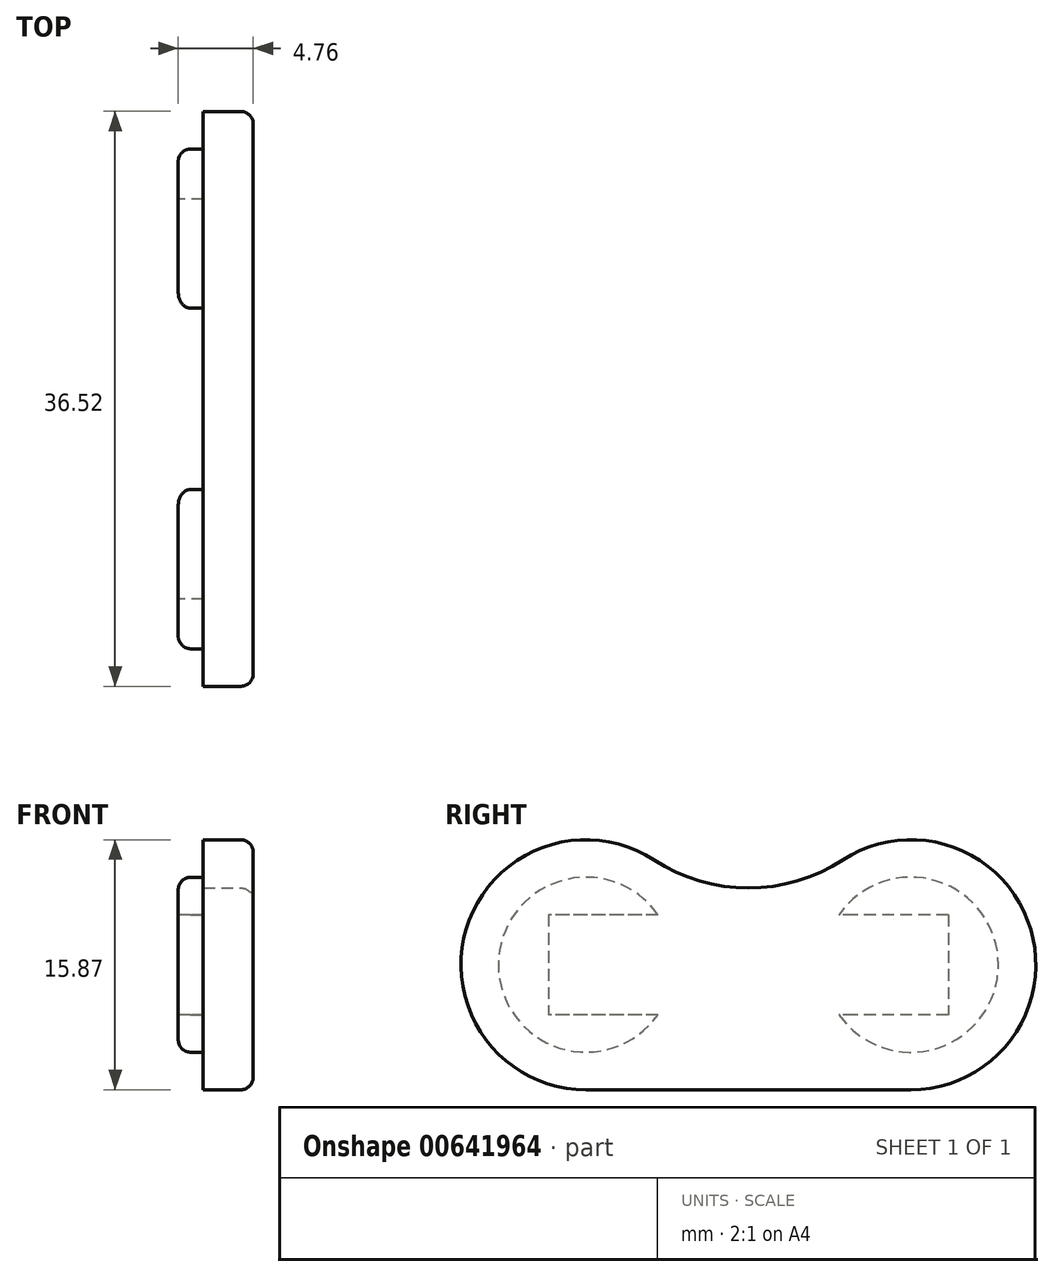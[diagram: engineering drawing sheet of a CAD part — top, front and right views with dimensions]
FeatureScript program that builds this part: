
annotation { "Feature Type Name" : "Feature", "Feature Type Description" : "" }
export const myFeature = defineFeature(function(context is Context, id is Id, definition is map)
    precondition{}
    {
        {
            var Q0;
            Q0=qCreatedBy(makeId("Right.planeOp"),FACE);
            var sketch = newSketch(context, id + "F0", { "sketchPlane" : qUnion([Q0])});
            skCircle(sketch, "E0", {"center": v(0, 0) * mm, "radius": 6.55 * mm});
            skCircle(sketch, "E1", {"center": v(0, 0) * mm, "radius": 8.73 * mm});
            skCircle(sketch, "E2", {"center": v(-10.32, -15.87) * mm, "radius": 5.56 * mm});
            skCircle(sketch, "E3", {"center": v(-10.32, -15.87) * mm, "radius": 7.94 * mm});
            skCircle(sketch, "E4", {"center": v(10.32, -15.87) * mm, "radius": 5.56 * mm});
            skCircle(sketch, "E5", {"center": v(10.32, -15.87) * mm, "radius": 7.94 * mm});
            skArc(sketch, "E6", {"start": v(-12.48, -8.24) * mm, "mid": v(-9.24, -5.77) * mm, "end": v(-8.55, -1.77) * mm});
            skArc(sketch, "E7", {"start": v(8.55, -1.77) * mm, "mid": v(9.24, -5.77) * mm, "end": v(12.48, -8.24) * mm});
            skLineSegment(sketch, "E8", {"start": v(-10.32, -23.81) * mm, "end": v(10.32, -23.81) * mm});
            skSolve(sketch);
        }
        {
            var Q0;
            Q0=makeQuery(id+"F0.imprint","IMPRINT",FACE,{"disambiguationData":[TD([[makeQuery(id+"F0.imprint","IMPRINT",EDGE,{"derivedFrom":sQuery(id+"F0.wireOp",EDGE,"E4")}),-1.0]])]});
            var Q1;
            Q1=makeQuery(id+"F0.imprint","IMPRINT",FACE,{"disambiguationData":[TD([[makeQuery(id+"F0.imprint","IMPRINT",EDGE,{"derivedFrom":sQuery(id+"F0.wireOp",EDGE,"E2")}),-1.0]])]});
            extrude(context, id + "F1", {"entities" : qUnion([Q0, Q1]), "depth" : 47.62 * mm, "offsetDistance" : 25.4 * mm});
        }
        {
            var Q0;
            Q0=makeQuery(id+"F0.imprint","IMPRINT",FACE,{"disambiguationData":[TD([[makeQuery(id+"F0.imprint","IMPRINT",EDGE,{"derivedFrom":sQuery(id+"F0.wireOp",EDGE,"E0")}),-1.0]])]});
            var Q1;
            {var subQ0=sQuery(id+"F0.wireOp",EDGE,"E3");var subQ1=sQuery(id+"F0.wireOp",EDGE,"E1");var subQ2=makeQuery(id+"F0.imprint","INTERSECT",VERTEX,{"disambiguationData":[OD(0.0)],"derivedFrom":[subQ1,subQ0]});Q1=makeQuery(id+"F0.imprint","IMPRINT",FACE,{"disambiguationData":[TD([[makeQuery(id+"F0.imprint","IMPRINT",EDGE,{"disambiguationData":[TD([[subQ2,-1.0]])],"derivedFrom":subQ1}),1.0]])]});}
            var Q2;
            {var subQ0=sQuery(id+"F0.wireOp",EDGE,"E5");var subQ1=sQuery(id+"F0.wireOp",EDGE,"E1");var subQ2=makeQuery(id+"F0.imprint","INTERSECT",VERTEX,{"disambiguationData":[OD(0.0)],"derivedFrom":[subQ1,subQ0]});Q2=makeQuery(id+"F0.imprint","IMPRINT",FACE,{"disambiguationData":[TD([[makeQuery(id+"F0.imprint","IMPRINT",EDGE,{"disambiguationData":[TD([[subQ2,-1.0]])],"derivedFrom":subQ1}),1.0]])]});}
            var Q3;
            {var subQ0=sQuery(id+"F0.wireOp",EDGE,"E6");Q3=makeQuery(id+"F0.imprint","IMPRINT",FACE,{"disambiguationData":[TD([[makeQuery(id+"F0.imprint","IMPRINT",EDGE,{"derivedFrom":subQ0}),-1.0]])]});}
            var Q4;
            {var subQ0=sQuery(id+"F0.wireOp",EDGE,"E7");Q4=makeQuery(id+"F0.imprint","IMPRINT",FACE,{"disambiguationData":[TD([[makeQuery(id+"F0.imprint","IMPRINT",EDGE,{"derivedFrom":subQ0}),-1.0]])]});}
            extrude(context, id + "F2", {"entities" : qUnion([Q0, Q1, Q2, Q3, Q4]), "operationType" : NewBodyOperationType.ADD, "depth" : 19.05 * mm, "offsetDistance" : 25.4 * mm});
        }
        {
            var Q0;
            Q0=makeQuery(id+"F1.opExtrude","CAP_FACE",FACE,{"disambiguationData":[OSD([sQuery(id+"F0.wireOp",EDGE,"E4"),sQuery(id+"F0.wireOp",EDGE,"E5")])],"isStart":false});
            var sketch = newSketch(context, id + "F3", { "sketchPlane" : qUnion([Q0])});
            skArc(sketch, "E9", {"start": v(-6, -9.22) * mm, "mid": v(0, -11) * mm, "end": v(6, -9.22) * mm});
            skCircle(sketch, "E10.0", {"center": v(10.32, -15.87) * mm, "radius": 7.94 * mm});
            skCircle(sketch, "E11.0", {"center": v(-10.32, -15.87) * mm, "radius": 7.94 * mm});
            skLineSegment(sketch, "E12.0", {"start": v(-10.32, -23.81) * mm, "end": v(10.32, -23.81) * mm});
            skSolve(sketch);
        }
        {
            var Q0;
            {var subQ0=sQuery(id+"F3.wireOp",EDGE,"E9");Q0=makeQuery(id+"F3.imprint","IMPRINT",FACE,{"disambiguationData":[TD([[makeQuery(id+"F3.imprint","IMPRINT",EDGE,{"derivedFrom":subQ0}),-1.0]])]});}
            extrude(context, id + "F4", {"entities" : qUnion([Q0]), "operationType" : NewBodyOperationType.ADD, "endBound" : BoundingType.UP_TO_NEXT, "oppositeDirection" : true, "depth" : 25.4 * mm, "offsetDistance" : 25.4 * mm});
        }
        {
            var Q0;
            {var subQ0=sQuery(id+"F0.wireOp",EDGE,"E5");var subQ1=sQuery(id+"F0.wireOp",EDGE,"E3");Q0=makeQuery(id+"F2.boolean.opBoolean","MERGE",FACE,{"derivedFrom":[makeQuery(id+"F1.opExtrude","CAP_FACE",FACE,{"disambiguationData":[OSD([sQuery(id+"F0.wireOp",EDGE,"E2"),subQ1])],"isStart":true}),makeQuery(id+"F1.opExtrude","CAP_FACE",FACE,{"disambiguationData":[OSD([sQuery(id+"F0.wireOp",EDGE,"E4"),subQ0])],"isStart":true}),makeQuery(id+"F2.opExtrude","CAP_FACE",FACE,{"disambiguationData":[OSD([sQuery(id+"F0.wireOp",EDGE,"E0"),sQuery(id+"F0.wireOp",EDGE,"E1"),subQ1,subQ0,sQuery(id+"F0.wireOp",EDGE,"E6"),sQuery(id+"F0.wireOp",EDGE,"E7"),sQuery(id+"F0.wireOp",EDGE,"E8")])],"isStart":true})]});}
            var sketch = newSketch(context, id + "F5", { "sketchPlane" : qUnion([Q0])});
            skLineSegment(sketch, "E13.bottom", {"start": v(4.37, -11.9) * mm, "end": v(-4.37, -11.9) * mm});
            skLineSegment(sketch, "E13.top", {"start": v(4.37, -20.64) * mm, "end": v(-4.37, -20.64) * mm});
            skLineSegment(sketch, "E13.left", {"start": v(4.37, -11.9) * mm, "end": v(4.37, -20.64) * mm});
            skLineSegment(sketch, "E13.right", {"start": v(-4.37, -11.9) * mm, "end": v(-4.37, -20.64) * mm});
            skPoint(sketch, "E13.middle", {"position": v(0, -16.27) * mm});
            skSolve(sketch);
        }
        {
            var Q0;
            {var subQ5=sQuery(id+"F5.wireOp",EDGE,"E13.bottom");Q0=makeQuery(id+"F5.imprint","IMPRINT",FACE,{"disambiguationData":[TD([[makeQuery(id+"F5.imprint","IMPRINT",EDGE,{"derivedFrom":subQ5}),1.0]])]});}
            extrude(context, id + "F6", {"entities" : qUnion([Q0]), "operationType" : NewBodyOperationType.REMOVE, "endBound" : BoundingType.THROUGH_ALL, "oppositeDirection" : true, "depth" : 25.4 * mm, "offsetDistance" : 25.4 * mm});
        }
        {
            var Q0;
            Q0=qCreatedBy(makeId("Front.planeOp"),FACE);
            var sketch = newSketch(context, id + "F7", { "sketchPlane" : qUnion([Q0])});
            skCircle(sketch, "E14", {"center": v(0, -16.27) * mm, "radius": 4.37 * mm});
            skCircle(sketch, "E15", {"center": v(47.63, -16.27) * mm, "radius": 4.37 * mm});
            skSolve(sketch);
        }
        {
            var Q0;
            Q0=makeQuery(id+"F7.imprint","IMPRINT",FACE,{"disambiguationData":[TD([[makeQuery(id+"F7.imprint","IMPRINT",EDGE,{"derivedFrom":sQuery(id+"F7.wireOp",EDGE,"E14")}),1.0]])]});
            var Q1;
            Q1=makeQuery(id+"F7.imprint","IMPRINT",FACE,{"disambiguationData":[TD([[makeQuery(id+"F7.imprint","IMPRINT",EDGE,{"derivedFrom":sQuery(id+"F7.wireOp",EDGE,"E15")}),1.0]])]});
            extrude(context, id + "F8", {"entities" : qUnion([Q0, Q1]), "operationType" : NewBodyOperationType.REMOVE, "oppositeDirection" : true, "depth" : 9.52 * mm, "offsetDistance" : 25.4 * mm, "hasSecondDirection" : true, "secondDirectionOppositeDirection" : false, "secondDirectionDepth" : 9.52 * mm});
        }
        {
            var Q0;
            Q0=makeQuery(id+"F6.boolean.opBoolean","COPY",FACE,{"derivedFrom":makeQuery(id+"F6.opExtrude","SWEPT_FACE",FACE,{"disambiguationData":[OSD([sQuery(id+"F5.wireOp",EDGE,"E13.bottom")])]})});
            var sketch = newSketch(context, id + "F9", { "sketchPlane" : qUnion([Q0])});
            skCircle(sketch, "E16", {"center": v(-0.51, 0) * mm, "radius": 4.37 * mm});
            skSolve(sketch);
        }
        {
            var Q0;
            {var subQ0=sQuery(id+"F9.wireOp",EDGE,"E16");var subQ1=makeQuery(id+"F6.boolean.opBoolean","COPY",EDGE,{"derivedFrom":makeQuery(id+"F6.opExtrude","CAP_EDGE",EDGE,{"disambiguationData":[OSD([sQuery(id+"F5.wireOp",EDGE,"E13.bottom")])],"isStart":true})});var subQ2=makeQuery(id+"F9.imprint","INTERSECT",VERTEX,{"disambiguationData":[OD(0.0)],"derivedFrom":[subQ1,subQ0]});Q0=makeQuery(id+"F9.imprint","IMPRINT",FACE,{"disambiguationData":[TD([[makeQuery(id+"F9.imprint","IMPRINT",EDGE,{"disambiguationData":[TD([[subQ2,1.0]])],"derivedFrom":subQ0}),1.0]])]});}
            var Q1;
            {var subQ0=sQuery(id+"F9.wireOp",EDGE,"E16");var subQ1=makeQuery(id+"F6.boolean.opBoolean","COPY",EDGE,{"derivedFrom":makeQuery(id+"F6.opExtrude","CAP_EDGE",EDGE,{"disambiguationData":[OSD([sQuery(id+"F5.wireOp",EDGE,"E13.bottom")])],"isStart":true})});var subQ2=makeQuery(id+"F9.imprint","INTERSECT",VERTEX,{"disambiguationData":[OD(0.0)],"derivedFrom":[subQ1,subQ0]});Q1=makeQuery(id+"F9.imprint","IMPRINT",FACE,{"disambiguationData":[TD([[makeQuery(id+"F9.imprint","IMPRINT",EDGE,{"disambiguationData":[TD([[subQ2,-1.0]])],"derivedFrom":subQ0}),1.0]])]});}
            extrude(context, id + "F10", {"entities" : qUnion([Q0, Q1]), "operationType" : NewBodyOperationType.REMOVE, "oppositeDirection" : true, "depth" : 9.52 * mm, "offsetDistance" : 25.4 * mm});
        }
        {
            var Q0;
            {var subQ0=sQuery(id+"F0.wireOp",EDGE,"E5");var subQ1=sQuery(id+"F0.wireOp",EDGE,"E3");Q0=makeQuery(id+"F2.boolean.opBoolean","MERGE",FACE,{"derivedFrom":[makeQuery(id+"F1.opExtrude","CAP_FACE",FACE,{"disambiguationData":[OSD([sQuery(id+"F0.wireOp",EDGE,"E2"),subQ1])],"isStart":true}),makeQuery(id+"F1.opExtrude","CAP_FACE",FACE,{"disambiguationData":[OSD([sQuery(id+"F0.wireOp",EDGE,"E4"),subQ0])],"isStart":true}),makeQuery(id+"F2.opExtrude","CAP_FACE",FACE,{"disambiguationData":[OSD([sQuery(id+"F0.wireOp",EDGE,"E0"),sQuery(id+"F0.wireOp",EDGE,"E1"),subQ1,subQ0,sQuery(id+"F0.wireOp",EDGE,"E6"),sQuery(id+"F0.wireOp",EDGE,"E7"),sQuery(id+"F0.wireOp",EDGE,"E8")])],"isStart":true})]});}
            var sketch = newSketch(context, id + "F11", { "sketchPlane" : qUnion([Q0])});
            skPoint(sketch, "E17", {"position": v(7.14, -7.94) * mm});
            skPoint(sketch, "E18", {"position": v(-7.14, -7.94) * mm});
            skSolve(sketch);
        }
        {
            var Q0;
            Q0=sQuery(id+"F11.wireOp",VERTEX,"E17");
            var Q1;
            Q1=sQuery(id+"F11.wireOp",VERTEX,"E18");
            var Q2;
            Q2=makeQuery(id+"F1.opExtrude","SWEPT_BODY",BODY,{"disambiguationData":[OSD([sQuery(id+"F0.wireOp",EDGE,"E2"),sQuery(id+"F0.wireOp",EDGE,"E3")])]});
            hole(context, id + "F12", {"style" : HoleStyle.SIMPLE, "endStyle" : HoleEndStyle.BLIND, "standardTappedOrClearance" : lookupTablePath({ "standard" : "ANSI", "engagement" : "75%", "pitch" : "32 tpi", "size" : "#6", "type" : "Tapped" }), "standardBlindInLast" : lookupTablePath({ "standard" : "ANSI", "engagement" : "75%", "pitch" : "32 tpi", "size" : "#6", "type" : "Tapped" }), "holeDiameter" : 2.7 * mm, "majorDiameter" : 3.5 * mm, "showTappedDepth" : true, "holeDepth" : 15.88 * mm, "isTappedThrough" : true, "tappedDepth" : 13.5 * mm, "tapClearance" : 3, "locations" : qUnion([Q0, Q1]), "scope" : qUnion([Q2])});
        }
        {
            var Q0;
            Q0=makeQuery(id+"F4.boolean.opBoolean","MERGE",FACE,{"derivedFrom":[makeQuery(id+"F1.opExtrude","CAP_FACE",FACE,{"disambiguationData":[OSD([sQuery(id+"F0.wireOp",EDGE,"E2"),sQuery(id+"F0.wireOp",EDGE,"E3")])],"isStart":false}),makeQuery(id+"F1.opExtrude","CAP_FACE",FACE,{"disambiguationData":[OSD([sQuery(id+"F0.wireOp",EDGE,"E4"),sQuery(id+"F0.wireOp",EDGE,"E5")])],"isStart":false}),makeQuery(id+"F4.opExtrude","CAP_FACE",FACE,{"disambiguationData":[OSD([sQuery(id+"F3.wireOp",EDGE,"E9"),sQuery(id+"F3.wireOp",EDGE,"E10.0"),sQuery(id+"F3.wireOp",EDGE,"E11.0"),sQuery(id+"F3.wireOp",EDGE,"E12.0")])],"isStart":true})]});
            var sketch = newSketch(context, id + "F13", { "sketchPlane" : qUnion([Q0])});
            skArc(sketch, "E19.0.0", {"start": v(-6, -9.22) * mm, "mid": v(-17.93, -13.62) * mm, "end": v(-10.32, -23.81) * mm});
            skLineSegment(sketch, "E19.0.1", {"start": v(-10.32, -23.81) * mm, "end": v(10.32, -23.81) * mm});
            skArc(sketch, "E19.0.2", {"start": v(10.32, -23.81) * mm, "mid": v(17.93, -13.62) * mm, "end": v(6, -9.22) * mm});
            skArc(sketch, "E19.0.3", {"start": v(6, -9.22) * mm, "mid": v(0, -11) * mm, "end": v(-6, -9.22) * mm});
            skSolve(sketch);
        }
        {
            var Q0;
            Q0=makeQuery(id+"F13.imprint","IMPRINT",FACE,{"disambiguationData":[TD([[makeQuery(id+"F13.imprint","IMPRINT",EDGE,{"derivedFrom":sQuery(id+"F13.wireOp",EDGE,"E19.0.0")}),1.0]])]});
            var Q1;
            {var subQ1=sQuery(id+"F0.wireOp",EDGE,"E2");Q1=makeQuery(id+"F13.imprint","IMPRINT",FACE,{"disambiguationData":[TD([[makeQuery(id+"F13.imprint","IMPRINT",EDGE,{"derivedFrom":makeQuery(id+"F1.opExtrude","CAP_EDGE",EDGE,{"disambiguationData":[OSD([subQ1])],"isStart":false})}),1.0]])]});}
            extrude(context, id + "F14", {"entities" : qUnion([Q0, Q1]), "operationType" : NewBodyOperationType.ADD, "depth" : 3.17 * mm, "offsetDistance" : 25.4 * mm});
        }
        {
            var Q0;
            Q0=qCreatedBy(makeId("Top.planeOp"),FACE);
            var sketch = newSketch(context, id + "F15", { "sketchPlane" : qUnion([Q0])});
            skLineSegment(sketch, "E20.bottom", {"start": v(47.62, 25.4) * mm, "end": v(-12.7, 25.4) * mm});
            skLineSegment(sketch, "E20.top", {"start": v(47.63, -25.4) * mm, "end": v(-12.7, -25.4) * mm});
            skLineSegment(sketch, "E20.left", {"start": v(47.63, 25.4) * mm, "end": v(47.63, -25.4) * mm});
            skLineSegment(sketch, "E20.right", {"start": v(-12.7, 25.4) * mm, "end": v(-12.7, -25.4) * mm});
            skSolve(sketch);
        }
        {
            var Q0;
            Q0=makeQuery(id+"F15.imprint","IMPRINT",FACE,{"disambiguationData":[TD([[makeQuery(id+"F15.imprint","IMPRINT",EDGE,{"derivedFrom":sQuery(id+"F15.wireOp",EDGE,"E20.bottom")}),1.0]])]});
            extrude(context, id + "F16", {"entities" : qUnion([Q0]), "operationType" : NewBodyOperationType.REMOVE, "oppositeDirection" : true, "depth" : 25.4 * mm, "offsetDistance" : 25.4 * mm, "hasSecondDirection" : true, "secondDirectionBound" : SecondDirectionBoundingType.THROUGH_ALL, "secondDirectionOppositeDirection" : false, "secondDirectionDepth" : 25.4 * mm});
        }
        {
            var Q0;
            Q0=makeQuery(id+"F13.imprint","IMPRINT",FACE,{"disambiguationData":[TD([[makeQuery(id+"F13.imprint","IMPRINT",EDGE,{"derivedFrom":sQuery(id+"F13.wireOp",EDGE,"E19.0.0")}),1.0]])]});
            var sketch = newSketch(context, id + "F17", { "sketchPlane" : qUnion([Q0])});
            skCircle(sketch, "E21.0", {"center": v(-10.32, -15.87) * mm, "radius": 5.56 * mm});
            skCircle(sketch, "E22.0", {"center": v(10.32, -15.87) * mm, "radius": 5.56 * mm});
            skSolve(sketch);
        }
        {
            var Q0;
            {var subQ0=sQuery(id+"F17.wireOp",EDGE,"E21.0");var subQ1=makeQuery(id+"F8.opExtrude","SWEPT_FACE",FACE,{"disambiguationData":[OSD([sQuery(id+"F7.wireOp",EDGE,"E15")])]});var subQ2=makeQuery(id+"F4.boolean.opBoolean","MERGE",FACE,{"derivedFrom":[makeQuery(id+"F1.opExtrude","CAP_FACE",FACE,{"disambiguationData":[OSD([sQuery(id+"F0.wireOp",EDGE,"E2"),sQuery(id+"F0.wireOp",EDGE,"E3")])],"isStart":false}),makeQuery(id+"F1.opExtrude","CAP_FACE",FACE,{"disambiguationData":[OSD([sQuery(id+"F0.wireOp",EDGE,"E4"),sQuery(id+"F0.wireOp",EDGE,"E5")])],"isStart":false}),makeQuery(id+"F4.opExtrude","CAP_FACE",FACE,{"disambiguationData":[OSD([sQuery(id+"F3.wireOp",EDGE,"E9"),sQuery(id+"F3.wireOp",EDGE,"E10.0"),sQuery(id+"F3.wireOp",EDGE,"E11.0"),sQuery(id+"F3.wireOp",EDGE,"E12.0")])],"isStart":true})]});var subQ3=makeQuery(id+"F17.imprint","INTERSECT",VERTEX,{"derivedFrom":[makeQuery(id+"F13.imprint","IMPRINT",EDGE,{"derivedFrom":makeQuery(id+"F8.boolean.opBoolean","INTERSECT",EDGE,{"disambiguationData":[OD(0.0)],"derivedFrom":[subQ2,subQ1]})}),subQ0]});Q0=makeQuery(id+"F17.imprint","IMPRINT",FACE,{"disambiguationData":[TD([[makeQuery(id+"F17.imprint","IMPRINT",EDGE,{"disambiguationData":[TD([[subQ3,1.0]])],"derivedFrom":subQ0}),1.0]])]});}
            var Q1;
            {var subQ0=sQuery(id+"F17.wireOp",EDGE,"E22.0");var subQ1=makeQuery(id+"F8.opExtrude","SWEPT_FACE",FACE,{"disambiguationData":[OSD([sQuery(id+"F7.wireOp",EDGE,"E15")])]});var subQ2=makeQuery(id+"F4.boolean.opBoolean","MERGE",FACE,{"derivedFrom":[makeQuery(id+"F1.opExtrude","CAP_FACE",FACE,{"disambiguationData":[OSD([sQuery(id+"F0.wireOp",EDGE,"E2"),sQuery(id+"F0.wireOp",EDGE,"E3")])],"isStart":false}),makeQuery(id+"F1.opExtrude","CAP_FACE",FACE,{"disambiguationData":[OSD([sQuery(id+"F0.wireOp",EDGE,"E4"),sQuery(id+"F0.wireOp",EDGE,"E5")])],"isStart":false}),makeQuery(id+"F4.opExtrude","CAP_FACE",FACE,{"disambiguationData":[OSD([sQuery(id+"F3.wireOp",EDGE,"E9"),sQuery(id+"F3.wireOp",EDGE,"E10.0"),sQuery(id+"F3.wireOp",EDGE,"E11.0"),sQuery(id+"F3.wireOp",EDGE,"E12.0")])],"isStart":true})]});var subQ3=makeQuery(id+"F17.imprint","INTERSECT",VERTEX,{"derivedFrom":[makeQuery(id+"F13.imprint","IMPRINT",EDGE,{"derivedFrom":makeQuery(id+"F8.boolean.opBoolean","INTERSECT",EDGE,{"disambiguationData":[OD(1.0)],"derivedFrom":[subQ2,subQ1]})}),subQ0]});Q1=makeQuery(id+"F17.imprint","IMPRINT",FACE,{"disambiguationData":[TD([[makeQuery(id+"F17.imprint","IMPRINT",EDGE,{"disambiguationData":[TD([[subQ3,-1.0]])],"derivedFrom":subQ0}),1.0]])]});}
            extrude(context, id + "F18", {"entities" : qUnion([Q0, Q1]), "operationType" : NewBodyOperationType.ADD, "oppositeDirection" : true, "depth" : 1.59 * mm, "offsetDistance" : 25.4 * mm});
        }
        {
            var Q0;
            Q0=makeQuery(id+"F18.opExtrude","CAP_EDGE",EDGE,{"disambiguationData":[OSD([sQuery(id+"F17.wireOp",EDGE,"E22.0")])],"isStart":false});
            var Q1;
            Q1=makeQuery(id+"F18.opExtrude","CAP_EDGE",EDGE,{"disambiguationData":[OSD([sQuery(id+"F17.wireOp",EDGE,"E21.0")])],"isStart":false});
            fillet(context, id + "F19", {"entities" : qUnion([Q0, Q1]), "radius" : 0.8 * mm, "tangentPropagation" : true, "allowEdgeOverflow" : false});
        }
        {
            var Q0;
            Q0=makeQuery(id+"F18.opExtrude","CAP_FACE",FACE,{"disambiguationData":[OSD([sQuery(id+"F17.wireOp",EDGE,"E21.0")])],"isStart":false});
            var sketch = newSketch(context, id + "F20", { "sketchPlane" : qUnion([Q0])});
            skLineSegment(sketch, "E23.bottom", {"start": v(-12.7, -12.7) * mm, "end": v(12.7, -12.7) * mm});
            skLineSegment(sketch, "E23.top", {"start": v(-12.7, -19.05) * mm, "end": v(12.7, -19.05) * mm});
            skLineSegment(sketch, "E23.left", {"start": v(-12.7, -12.7) * mm, "end": v(-12.7, -19.05) * mm});
            skLineSegment(sketch, "E23.right", {"start": v(12.7, -12.7) * mm, "end": v(12.7, -19.05) * mm});
            skSolve(sketch);
        }
        {
            var Q0;
            {var subQ0=sQuery(id+"F20.wireOp",EDGE,"E23.left");Q0=makeQuery(id+"F20.imprint","IMPRINT",FACE,{"disambiguationData":[TD([[makeQuery(id+"F20.imprint","IMPRINT",EDGE,{"derivedFrom":subQ0}),1.0]])]});}
            var Q1;
            {var subQ0=sQuery(id+"F20.wireOp",EDGE,"E23.right");Q1=makeQuery(id+"F20.imprint","IMPRINT",FACE,{"disambiguationData":[TD([[makeQuery(id+"F20.imprint","IMPRINT",EDGE,{"derivedFrom":subQ0}),-1.0]])]});}
            extrude(context, id + "F21", {"entities" : qUnion([Q0, Q1]), "operationType" : NewBodyOperationType.REMOVE, "oppositeDirection" : true, "depth" : 1.59 * mm, "offsetDistance" : 25.4 * mm});
        }
        {
            var Q0;
            Q0=makeQuery(id+"F14.opExtrude","CAP_EDGE",EDGE,{"disambiguationData":[OSD([sQuery(id+"F13.wireOp",EDGE,"E19.0.2")])],"isStart":false});
            fillet(context, id + "F22", {"entities" : qUnion([Q0]), "radius" : 0.8 * mm, "tangentPropagation" : true, "allowEdgeOverflow" : false});
        }
    });
